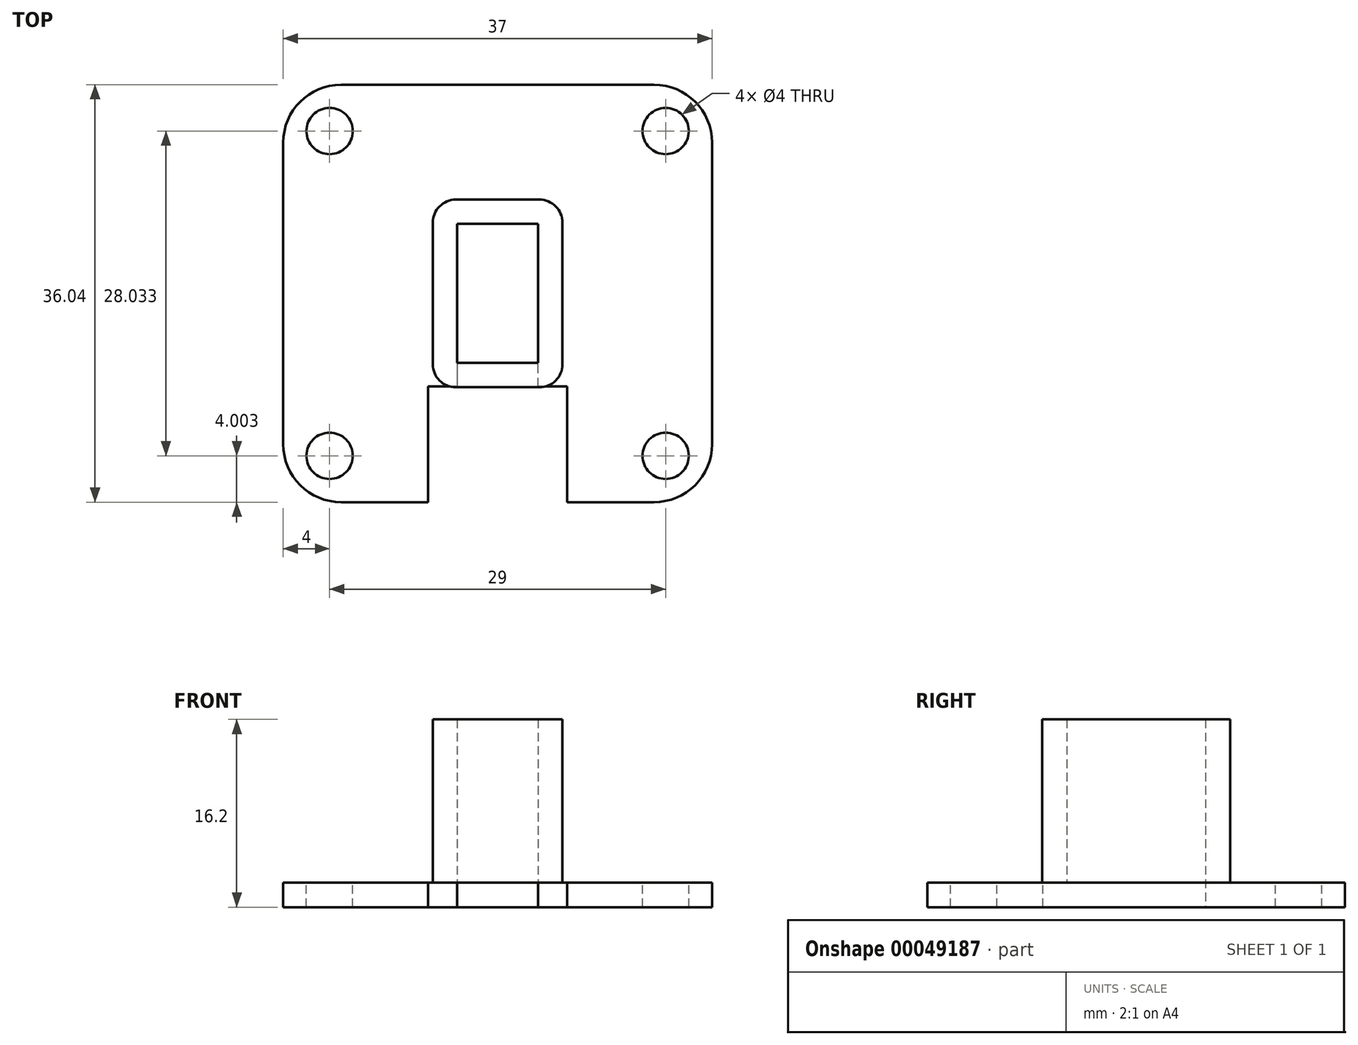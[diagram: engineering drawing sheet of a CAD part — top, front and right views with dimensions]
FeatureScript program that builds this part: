
annotation { "Feature Type Name" : "Feature", "Feature Type Description" : "" }
export const myFeature = defineFeature(function(context is Context, id is Id, definition is map)
    precondition{}
    {
        {
            var Q0;
            Q0=qCreatedBy(makeId("Top.planeOp"),FACE);
            var sketch = newSketch(context, id + "F0", { "sketchPlane" : qUnion([Q0])});
            skLineSegment(sketch, "E0.rect.bottom", {"start": v(-3.5, -6) * mm, "end": v(3.5, -6) * mm});
            skLineSegment(sketch, "E0.rect.top", {"start": v(-3.5, 6) * mm, "end": v(3.5, 6) * mm});
            skLineSegment(sketch, "E0.rect.left", {"start": v(-3.5, -6) * mm, "end": v(-3.5, 6) * mm});
            skLineSegment(sketch, "E0.rect.right", {"start": v(3.5, -6) * mm, "end": v(3.5, 6) * mm});
            skPoint(sketch, "E0.rect.middle", {"position": v(0, 0) * mm});
            skLineSegment(sketch, "E1.rect.bottom", {"start": v(5.6, -8.1) * mm, "end": v(-5.6, -8.1) * mm});
            skLineSegment(sketch, "E1.rect.top", {"start": v(5.6, 8.1) * mm, "end": v(-5.6, 8.1) * mm});
            skLineSegment(sketch, "E1.rect.left", {"start": v(5.6, -8.1) * mm, "end": v(5.6, 8.1) * mm});
            skLineSegment(sketch, "E1.rect.right", {"start": v(-5.6, -8.1) * mm, "end": v(-5.6, 8.1) * mm});
            skSolve(sketch);
        }
        {
            var Q0;
            Q0 = qSketchRegion(id + "F0", true);
            extrude(context, id + "F1", {"entities" : qUnion([Q0]), "depth" : 14.1 * mm});
        }
        {
            var Q0;
            Q0=qCreatedBy(makeId("Top.planeOp"),FACE);
            var sketch = newSketch(context, id + "F2", { "sketchPlane" : qUnion([Q0])});
            skLineSegment(sketch, "E2.rect.bottom", {"start": v(18.5, -18.02) * mm, "end": v(-18.5, -18.02) * mm});
            skLineSegment(sketch, "E2.rect.top", {"start": v(18.5, 18.02) * mm, "end": v(-18.5, 18.02) * mm});
            skLineSegment(sketch, "E2.rect.left", {"start": v(18.5, -18.02) * mm, "end": v(18.5, 18.02) * mm});
            skLineSegment(sketch, "E2.rect.right", {"start": v(-18.5, -18.02) * mm, "end": v(-18.5, 18.02) * mm});
            skPoint(sketch, "E2.rect.middle", {"position": v(0, 0) * mm});
            skLineSegment(sketch, "E3.bottom", {"start": v(-18.5, -18.02) * mm, "end": v(-14.5, -18.02) * mm});
            skLineSegment(sketch, "E3.left", {"start": v(-18.5, -18.02) * mm, "end": v(-18.5, -14.02) * mm});
            skCircle(sketch, "E4", {"center": v(-14.5, -14.02) * mm, "radius": 2 * mm});
            skLineSegment(sketch, "E5", {"start": v(0, -18.02) * mm, "end": v(0, -15.96) * mm});
            skPoint(sketch, "E5.endSnap0", {"position": v(0, -18.02) * mm});
            skLineSegment(sketch, "E6", {"start": v(-18.5, 0) * mm, "end": v(-16.2, 0) * mm});
            skPoint(sketch, "E6.endSnap0", {"position": v(-18.5, 0) * mm});
            skCircle(sketch, "E7.MirrorC", {"center": v(14.5, -14.02) * mm, "radius": 2 * mm});
            skLineSegment(sketch, "E8.MirrorCS", {"start": v(18.5, 0) * mm, "end": v(16.2, 0) * mm});
            skCircle(sketch, "E9.MirrorC", {"center": v(14.5, 14.02) * mm, "radius": 2 * mm});
            skPoint(sketch, "E10.MirrorP", {"position": v(0, 18.02) * mm});
            skCircle(sketch, "E11.MirrorC", {"center": v(-14.5, 14.02) * mm, "radius": 2 * mm});
            skLineSegment(sketch, "E12.rect.bottom", {"start": v(3.5, -6) * mm, "end": v(-3.5, -6) * mm});
            skLineSegment(sketch, "E12.rect.top", {"start": v(3.5, 6) * mm, "end": v(-3.5, 6) * mm});
            skLineSegment(sketch, "E12.rect.left", {"start": v(3.5, -6) * mm, "end": v(3.5, 6) * mm});
            skLineSegment(sketch, "E12.rect.right", {"start": v(-3.5, -6) * mm, "end": v(-3.5, 6) * mm});
            skLineSegment(sketch, "E13.bottom", {"start": v(-3.5, 0) * mm, "end": v(3.5, 0) * mm});
            skLineSegment(sketch, "E13.top", {"start": v(-3.5, -18.02) * mm, "end": v(3.5, -18.02) * mm});
            skLineSegment(sketch, "E13.left", {"start": v(-3.5, 0) * mm, "end": v(-3.5, -6) * mm});
            skLineSegment(sketch, "E13.right", {"start": v(3.5, 0) * mm, "end": v(3.5, -6) * mm});
            skLineSegment(sketch, "E14", {"start": v(0, 0) * mm, "end": v(3.5, 0) * mm});
            skLineSegment(sketch, "E15", {"start": v(0, 0) * mm, "end": v(-3.5, 0) * mm});
            skLineSegment(sketch, "E16", {"start": v(6, -8.04) * mm, "end": v(6, -18.02) * mm});
            skLineSegment(sketch, "E17", {"start": v(-6, -8.04) * mm, "end": v(-6, -18.02) * mm});
            skLineSegment(sketch, "E18", {"start": v(-3.5, -6) * mm, "end": v(-3.5, -8.04) * mm});
            skLineSegment(sketch, "E19", {"start": v(-3.5, -8.04) * mm, "end": v(-6, -8.04) * mm});
            skLineSegment(sketch, "E20", {"start": v(6, -8.04) * mm, "end": v(3.5, -8.04) * mm});
            skLineSegment(sketch, "E21", {"start": v(3.5, -8.04) * mm, "end": v(3.5, -6) * mm});
            skSolve(sketch);
        }
        {
            var Q0;
            {var subQ13=sQuery(id+"F2.wireOp",EDGE,"E2.rect.top");Q0=makeQuery(id+"F2.imprint","IMPRINT",FACE,{"disambiguationData":[TD([[makeQuery(id+"F2.imprint","IMPRINT",EDGE,{"derivedFrom":subQ13}),1.0]])]});}
            extrude(context, id + "F3", {"entities" : qUnion([Q0]), "operationType" : NewBodyOperationType.ADD, "oppositeDirection" : true, "depth" : 2.1 * mm});
        }
        {
            var Q0;
            Q0=makeQuery(id+"F3.opExtrude","SWEPT_EDGE",EDGE,{"disambiguationData":[OSD([sQuery(id+"F2.wireOp",EDGE,"E2.rect.top"),sQuery(id+"F2.wireOp",EDGE,"E2.rect.right")])]});
            var Q1;
            Q1=makeQuery(id+"F3.opExtrude","SWEPT_EDGE",EDGE,{"disambiguationData":[OSD([sQuery(id+"F2.wireOp",EDGE,"E2.rect.top"),sQuery(id+"F2.wireOp",EDGE,"E2.rect.left")])]});
            var Q2;
            Q2=makeQuery(id+"F3.opExtrude","SWEPT_EDGE",EDGE,{"disambiguationData":[OSD([sQuery(id+"F2.wireOp",EDGE,"E2.rect.bottom"),sQuery(id+"F2.wireOp",EDGE,"E2.rect.left")])]});
            var Q3;
            Q3=makeQuery(id+"F3.opExtrude","SWEPT_EDGE",EDGE,{"disambiguationData":[OSD([sQuery(id+"F2.wireOp",EDGE,"E2.rect.bottom"),sQuery(id+"F2.wireOp",EDGE,"E2.rect.right")])]});
            var Q4;
            Q4=makeQuery(id+"F3.opExtrude","SWEPT_EDGE",EDGE,{"disambiguationData":[OSD([sQuery(id+"F2.wireOp",EDGE,"E3.bottom"),sQuery(id+"F2.wireOp",EDGE,"E3.left")])]});
            fillet(context, id + "F4", {"entities" : qUnion([Q0, Q1, Q2, Q3, Q4]), "radius" : 5 * mm, "tangentPropagation" : true, "allowEdgeOverflow" : false});
        }
        {
            var Q0;
            Q0=makeQuery(id+"F1.opExtrude","SWEPT_EDGE",EDGE,{"disambiguationData":[OSD([sQuery(id+"F0.wireOp",EDGE,"E1.rect.top"),sQuery(id+"F0.wireOp",EDGE,"E1.rect.left")])]});
            var Q1;
            Q1=makeQuery(id+"F1.opExtrude","SWEPT_EDGE",EDGE,{"disambiguationData":[OSD([sQuery(id+"F0.wireOp",EDGE,"E1.rect.top"),sQuery(id+"F0.wireOp",EDGE,"E1.rect.right")])]});
            var Q2;
            Q2=makeQuery(id+"F1.opExtrude","SWEPT_EDGE",EDGE,{"disambiguationData":[OSD([sQuery(id+"F0.wireOp",EDGE,"E1.rect.bottom"),sQuery(id+"F0.wireOp",EDGE,"E1.rect.left")])]});
            var Q3;
            Q3=makeQuery(id+"F1.opExtrude","SWEPT_EDGE",EDGE,{"disambiguationData":[OSD([sQuery(id+"F0.wireOp",EDGE,"E1.rect.bottom"),sQuery(id+"F0.wireOp",EDGE,"E1.rect.right")])]});
            fillet(context, id + "F5", {"entities" : qUnion([Q0, Q1, Q2, Q3]), "radius" : 2 * mm, "tangentPropagation" : true, "allowEdgeOverflow" : false});
        }
    });
